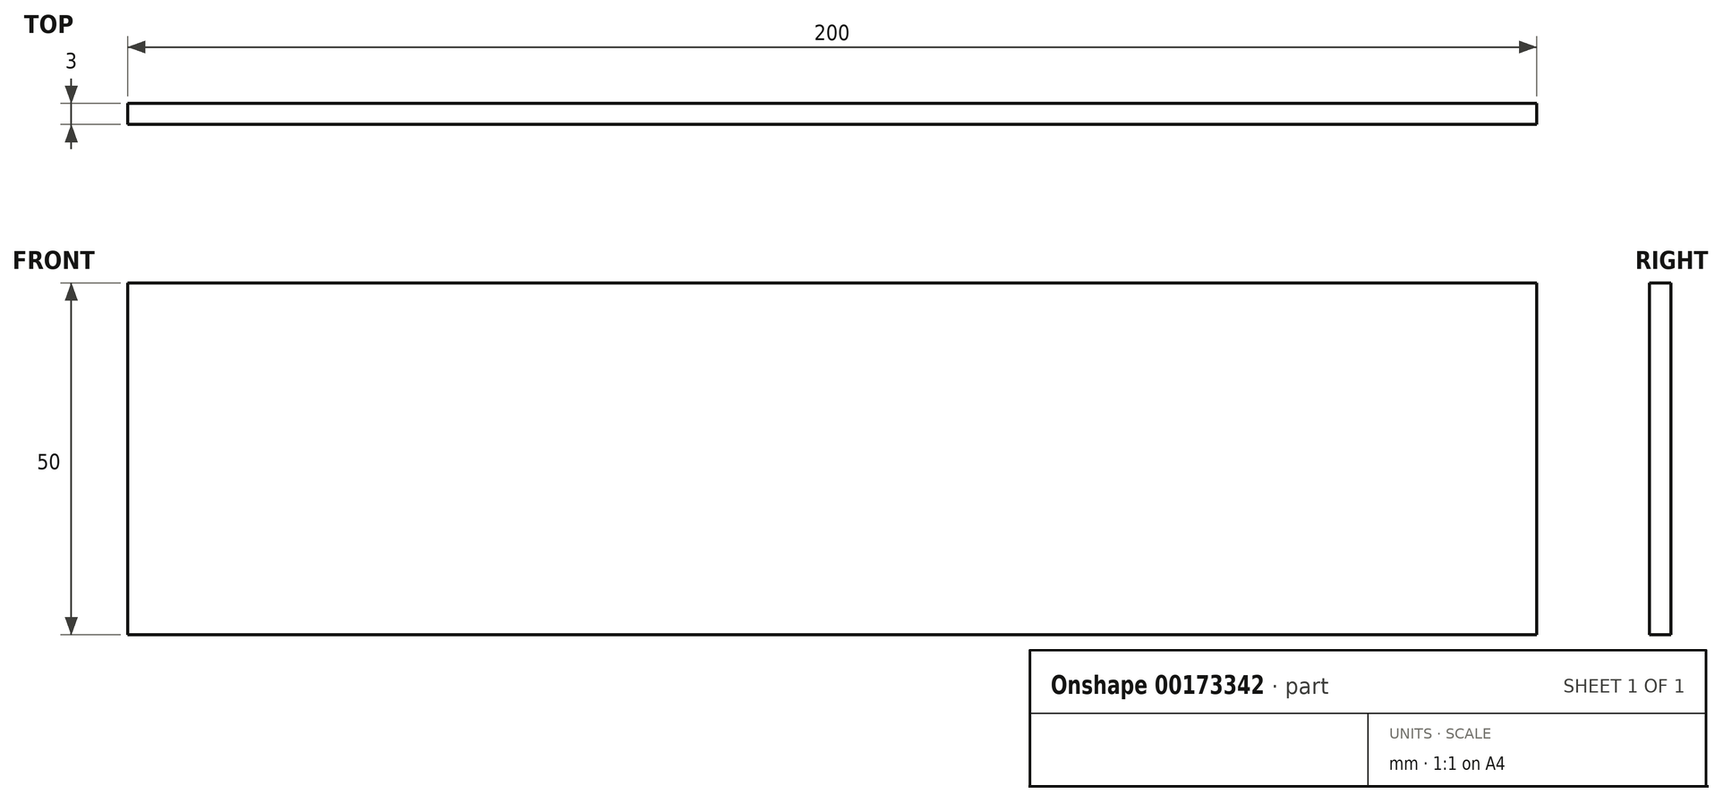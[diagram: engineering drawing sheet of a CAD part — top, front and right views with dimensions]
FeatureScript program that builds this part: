
annotation { "Feature Type Name" : "Feature", "Feature Type Description" : "" }
export const myFeature = defineFeature(function(context is Context, id is Id, definition is map)
    precondition{}
    {
        {
            var Q0;
            Q0=qCreatedBy(makeId("Front.planeOp"),FACE);
            var sketch = newSketch(context, id + "F0", { "sketchPlane" : qUnion([Q0])});
            skLineSegment(sketch, "E0.bottom", {"start": v(-100, 25) * mm, "end": v(100, 25) * mm});
            skLineSegment(sketch, "E0.top", {"start": v(-100, -25) * mm, "end": v(100, -25) * mm});
            skLineSegment(sketch, "E0.left", {"start": v(-100, 25) * mm, "end": v(-100, -25) * mm});
            skLineSegment(sketch, "E0.right", {"start": v(100, 25) * mm, "end": v(100, -25) * mm});
            skSolve(sketch);
        }
        {
            var Q0;
            Q0 = qSketchRegion(id + "F0", true);
            extrude(context, id + "F1", {"entities" : qUnion([Q0]), "endBound" : BoundingType.SYMMETRIC, "depth" : 3 * mm});
        }
    });
